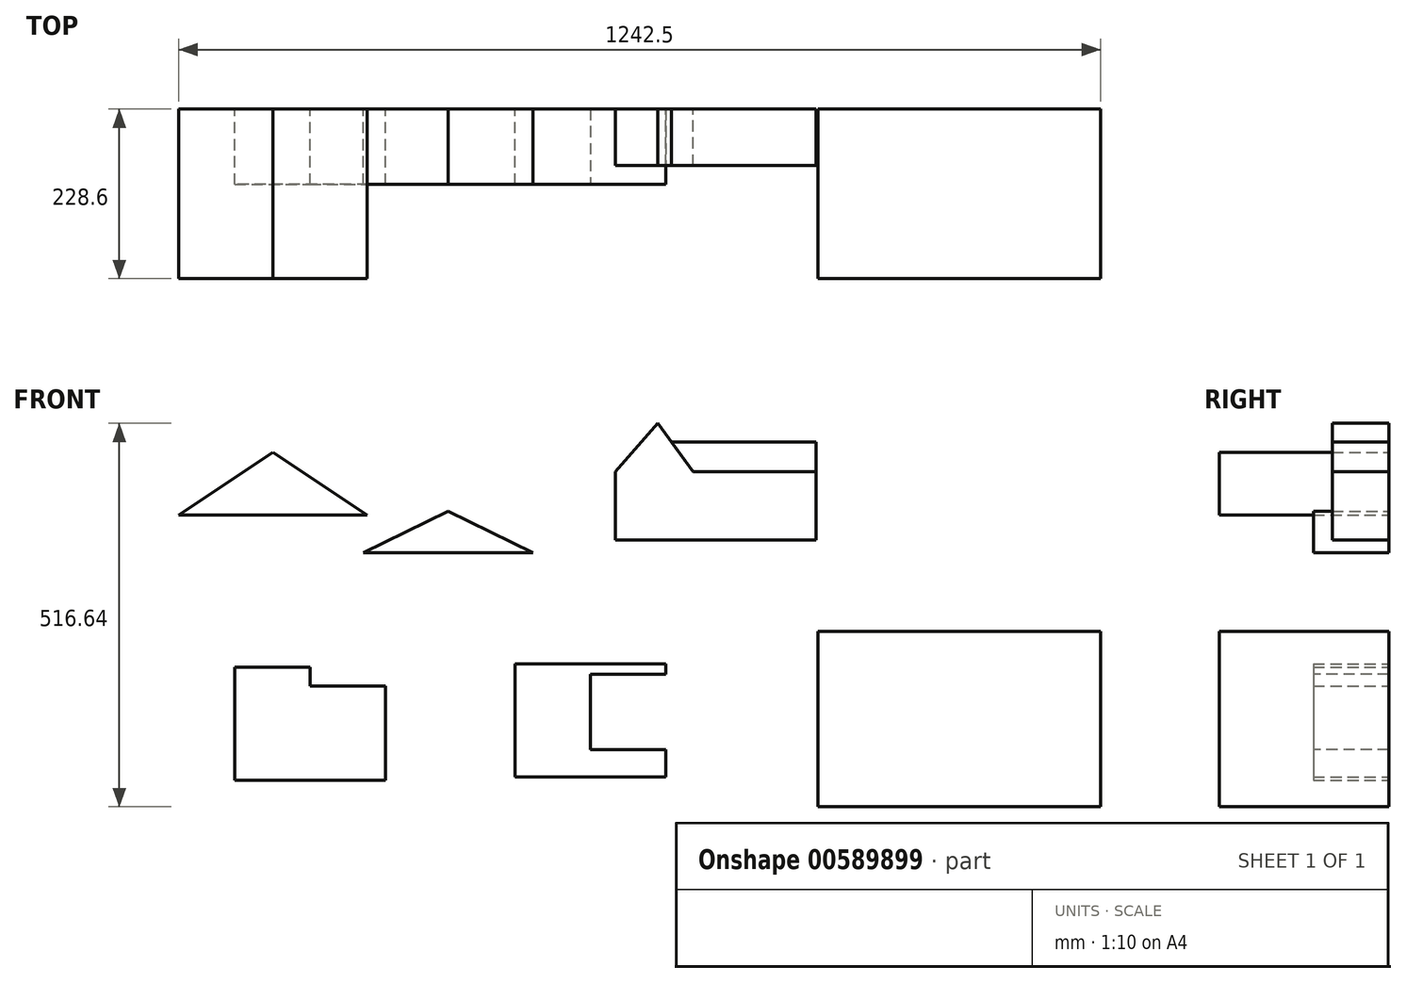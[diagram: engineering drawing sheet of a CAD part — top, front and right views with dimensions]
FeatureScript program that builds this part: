
annotation { "Feature Type Name" : "Feature", "Feature Type Description" : "" }
export const myFeature = defineFeature(function(context is Context, id is Id, definition is map)
    precondition{}
    {
        {
            var Q0;
            Q0=qCreatedBy(makeId("Front.planeOp"),FACE);
            var sketch = newSketch(context, id + "F0", { "sketchPlane" : qUnion([Q0])});
            skLineSegment(sketch, "E0", {"start": v(68.06, -35.27) * mm, "end": v(195.06, 48.97) * mm});
            skLineSegment(sketch, "E1", {"start": v(68.06, -35.27) * mm, "end": v(322.06, -35.27) * mm});
            skLineSegment(sketch, "E2", {"start": v(322.06, -35.27) * mm, "end": v(195.06, 48.97) * mm});
            skSolve(sketch);
        }
        {
            var Q0;
            Q0 = qSketchRegion(id + "F0", true);
            extrude(context, id + "F1", {"entities" : qUnion([Q0]), "depth" : 127 * mm, "offsetDistance" : 25.4 * mm});
        }
        {
            var Q0;
            Q0=makeQuery(id+"F1.opExtrude","CAP_FACE",FACE,{"disambiguationData":[OSD([sQuery(id+"F0.wireOp",EDGE,"E0"),sQuery(id+"F0.wireOp",EDGE,"E1"),sQuery(id+"F0.wireOp",EDGE,"E2")])],"isStart":false});
            var sketch = newSketch(context, id + "F2", { "sketchPlane" : qUnion([Q0])});
            skSolve(sketch);
        }
        {
            var Q0;
            Q0=makeQuery(id+"F2.imprint","IMPRINT",FACE,{"disambiguationData":[TD([[makeQuery(id+"F2.imprint","IMPRINT",EDGE,{"derivedFrom":makeQuery(id+"F1.opExtrude","CAP_EDGE",EDGE,{"disambiguationData":[OSD([sQuery(id+"F0.wireOp",EDGE,"E0")])],"isStart":false})}),-1.0]])]});
            var sketch = newSketch(context, id + "F3", { "sketchPlane" : qUnion([Q0])});
            skLineSegment(sketch, "E3", {"start": v(151.57, 21.29) * mm, "end": v(237, 21.29) * mm});
            skSolve(sketch);
        }
        {
            var Q0;
            Q0 = qSketchRegion(id + "F3", true);
            var Q1;
            Q1=makeQuery(id+"F2.imprint","IMPRINT",FACE,{"disambiguationData":[TD([[makeQuery(id+"F2.imprint","IMPRINT",EDGE,{"derivedFrom":makeQuery(id+"F1.opExtrude","CAP_EDGE",EDGE,{"disambiguationData":[OSD([sQuery(id+"F0.wireOp",EDGE,"E0")])],"isStart":false})}),-1.0]])]});
            extrude(context, id + "F4", {"entities" : qUnion([Q0, Q1]), "operationType" : NewBodyOperationType.ADD, "depth" : 76.2 * mm, "offsetDistance" : 25.4 * mm});
        }
        {
            var Q0;
            Q0=makeQuery(id+"F4.opExtrude","CAP_FACE",FACE,{"disambiguationData":[OSD([sQuery(id+"F0.wireOp",EDGE,"E0"),sQuery(id+"F0.wireOp",EDGE,"E1"),sQuery(id+"F0.wireOp",EDGE,"E2")])],"isStart":false});
            var sketch = newSketch(context, id + "F5", { "sketchPlane" : qUnion([Q0])});
            skSolve(sketch);
        }
        {
            var Q0;
            Q0 = qSketchRegion(id + "F5", true);
            var Q1;
            Q1=makeQuery(id+"F5.imprint","IMPRINT",FACE,{"disambiguationData":[TD([[makeQuery(id+"F5.imprint","IMPRINT",EDGE,{"derivedFrom":makeQuery(id+"F4.opExtrude","CAP_EDGE",EDGE,{"disambiguationData":[OSD([sQuery(id+"F0.wireOp",EDGE,"E0")])],"isStart":false})}),-1.0]])]});
            extrude(context, id + "F6", {"entities" : qUnion([Q0, Q1]), "operationType" : NewBodyOperationType.ADD, "depth" : 25.4 * mm, "offsetDistance" : 25.4 * mm});
        }
        {
            var Q0;
            Q0=qCreatedBy(makeId("Front.planeOp"),FACE);
            var sketch = newSketch(context, id + "F7", { "sketchPlane" : qUnion([Q0])});
            skLineSegment(sketch, "E4", {"start": v(431.32, -30.58) * mm, "end": v(317.02, -85.94) * mm});
            skLineSegment(sketch, "E5", {"start": v(431.32, -30.58) * mm, "end": v(545.62, -85.94) * mm});
            skLineSegment(sketch, "E6", {"start": v(545.62, -85.94) * mm, "end": v(317.02, -85.94) * mm});
            skSolve(sketch);
        }
        {
            var Q0;
            Q0 = qSketchRegion(id + "F7", true);
            extrude(context, id + "F8", {"entities" : qUnion([Q0]), "depth" : 101.6 * mm, "offsetDistance" : 25.4 * mm});
        }
        {
            var Q0;
            Q0=qCreatedBy(makeId("Front.planeOp"),FACE);
            var sketch = newSketch(context, id + "F9", { "sketchPlane" : qUnion([Q0])});
            skLineSegment(sketch, "E7", {"start": v(656.84, 22.7) * mm, "end": v(656.84, -69.03) * mm});
            skLineSegment(sketch, "E8", {"start": v(656.84, -69.03) * mm, "end": v(927.34, -69.03) * mm});
            skLineSegment(sketch, "E9", {"start": v(927.34, -69.03) * mm, "end": v(927.34, 84.7) * mm});
            skLineSegment(sketch, "E10", {"start": v(656.84, 22.7) * mm, "end": v(713.94, 88.22) * mm});
            skLineSegment(sketch, "E11", {"start": v(713.94, 88.22) * mm, "end": v(761.67, 22.7) * mm});
            skLineSegment(sketch, "E12", {"start": v(732.1, 63.3) * mm, "end": v(927.34, 63.3) * mm});
            skLineSegment(sketch, "E13", {"start": v(761.67, 22.7) * mm, "end": v(927.34, 22.7) * mm});
            skLineSegment(sketch, "E14", {"start": v(761.67, 22.7) * mm, "end": v(761.67, -69.03) * mm});
            skSolve(sketch);
        }
        {
            var Q0;
            {var subQ0=sQuery(id+"F9.wireOp",EDGE,"E12");Q0=makeQuery(id+"F9.imprint","IMPRINT",FACE,{"disambiguationData":[TD([[makeQuery(id+"F9.imprint","IMPRINT",EDGE,{"derivedFrom":subQ0}),-1.0]])]});}
            var sketch = newSketch(context, id + "F10", { "sketchPlane" : qUnion([Q0])});
            skSolve(sketch);
        }
        {
            var Q0;
            {var subQ4=sQuery(id+"F9.wireOp",EDGE,"E13");Q0=makeQuery(id+"F9.imprint","IMPRINT",FACE,{"disambiguationData":[TD([[makeQuery(id+"F9.imprint","IMPRINT",EDGE,{"derivedFrom":subQ4}),-1.0]])]});}
            var Q1;
            {var subQ4=sQuery(id+"F9.wireOp",EDGE,"E7");Q1=makeQuery(id+"F9.imprint","IMPRINT",FACE,{"disambiguationData":[TD([[makeQuery(id+"F9.imprint","IMPRINT",EDGE,{"derivedFrom":subQ4}),1.0]])]});}
            var Q2;
            {var subQ0=sQuery(id+"F9.wireOp",EDGE,"E12");Q2=makeQuery(id+"F10.imprint","IMPRINT",FACE,{"disambiguationData":[TD([[makeQuery(id+"F10.imprint","IMPRINT",EDGE,{"derivedFrom":makeQuery(id+"F9.imprint","IMPRINT",EDGE,{"derivedFrom":subQ0})}),-1.0]])]});}
            extrude(context, id + "F11", {"entities" : qUnion([Q0, Q1, Q2]), "depth" : 76.2 * mm, "offsetDistance" : 25.4 * mm});
        }
        {
            var Q0;
            Q0=qCreatedBy(makeId("Front.planeOp"),FACE);
            var sketch = newSketch(context, id + "F12", { "sketchPlane" : qUnion([Q0])});
            skLineSegment(sketch, "E15", {"start": v(143.28, -240.65) * mm, "end": v(143.28, -393.05) * mm});
            skLineSegment(sketch, "E16", {"start": v(143.28, -240.65) * mm, "end": v(244.88, -240.65) * mm});
            skLineSegment(sketch, "E17", {"start": v(244.88, -240.65) * mm, "end": v(244.88, -266.05) * mm});
            skLineSegment(sketch, "E18", {"start": v(244.88, -266.05) * mm, "end": v(346.48, -266.05) * mm});
            skLineSegment(sketch, "E19", {"start": v(346.48, -266.05) * mm, "end": v(346.48, -393.05) * mm});
            skLineSegment(sketch, "E20", {"start": v(346.48, -393.05) * mm, "end": v(143.28, -393.05) * mm});
            skSolve(sketch);
        }
        {
            var Q0;
            Q0 = qSketchRegion(id + "F12", true);
            extrude(context, id + "F13", {"entities" : qUnion([Q0]), "depth" : 101.6 * mm, "offsetDistance" : 25.4 * mm});
        }
        {
            var Q0;
            Q0=qCreatedBy(makeId("Front.planeOp"),FACE);
            var sketch = newSketch(context, id + "F14", { "sketchPlane" : qUnion([Q0])});
            skLineSegment(sketch, "E21.bottom", {"start": v(521.15, -236.11) * mm, "end": v(724.35, -236.11) * mm});
            skLineSegment(sketch, "E21.top", {"start": v(521.15, -388.51) * mm, "end": v(724.35, -388.51) * mm});
            skLineSegment(sketch, "E21.left", {"start": v(521.15, -236.11) * mm, "end": v(521.15, -388.51) * mm});
            skLineSegment(sketch, "E21.right", {"start": v(724.35, -236.11) * mm, "end": v(724.35, -388.51) * mm});
            skLineSegment(sketch, "E22", {"start": v(724.35, -259.36) * mm, "end": v(622.75, -259.36) * mm});
            skLineSegment(sketch, "E23", {"start": v(622.75, -259.36) * mm, "end": v(622.75, -360.96) * mm});
            skLineSegment(sketch, "E24", {"start": v(622.75, -360.96) * mm, "end": v(724.35, -360.96) * mm});
            skSolve(sketch);
        }
        {
            var Q0;
            {var subQ1=sQuery(id+"F14.wireOp",EDGE,"E21.bottom");Q0=makeQuery(id+"F14.imprint","IMPRINT",FACE,{"disambiguationData":[TD([[makeQuery(id+"F14.imprint","IMPRINT",EDGE,{"derivedFrom":subQ1}),-1.0]])]});}
            var Q1;
            {var subQ0=sQuery(id+"F14.wireOp",EDGE,"E22");Q1=makeQuery(id+"F14.imprint","IMPRINT",FACE,{"disambiguationData":[TD([[makeQuery(id+"F14.imprint","IMPRINT",EDGE,{"derivedFrom":subQ0}),1.0]])]});}
            extrude(context, id + "F15", {"entities" : qUnion([Q0, Q1]), "depth" : 101.6 * mm, "offsetDistance" : 25.4 * mm});
        }
        {
            var Q0;
            Q0=makeQuery(id+"F15.opExtrude","CAP_FACE",FACE,{"disambiguationData":[OSD([sQuery(id+"F14.wireOp",EDGE,"E21.bottom"),sQuery(id+"F14.wireOp",EDGE,"E21.top"),sQuery(id+"F14.wireOp",EDGE,"E21.left"),sQuery(id+"F14.wireOp",EDGE,"E21.right")])],"isStart":false});
            var sketch = newSketch(context, id + "F16", { "sketchPlane" : qUnion([Q0])});
            skLineSegment(sketch, "E25", {"start": v(724.35, -250.35) * mm, "end": v(622.75, -250.35) * mm});
            skLineSegment(sketch, "E26", {"start": v(622.75, -250.35) * mm, "end": v(622.75, -351.95) * mm});
            skLineSegment(sketch, "E27", {"start": v(622.75, -351.95) * mm, "end": v(724.35, -351.95) * mm});
            skSolve(sketch);
        }
        {
            var Q0;
            {var subQ0=sQuery(id+"F16.wireOp",EDGE,"E25");Q0=makeQuery(id+"F16.imprint","IMPRINT",FACE,{"disambiguationData":[TD([[makeQuery(id+"F16.imprint","IMPRINT",EDGE,{"derivedFrom":subQ0}),1.0]])]});}
            extrude(context, id + "F17", {"entities" : qUnion([Q0]), "operationType" : NewBodyOperationType.REMOVE, "oppositeDirection" : true, "depth" : 127 * mm, "offsetDistance" : 25.4 * mm});
        }
        {
            var Q0;
            Q0=qCreatedBy(makeId("Front.planeOp"),FACE);
            var sketch = newSketch(context, id + "F18", { "sketchPlane" : qUnion([Q0])});
            skLineSegment(sketch, "E28.bottom", {"start": v(929.42, -192.48) * mm, "end": v(1310.56, -192.48) * mm});
            skLineSegment(sketch, "E28.top", {"start": v(929.42, -428.42) * mm, "end": v(1310.56, -428.42) * mm});
            skLineSegment(sketch, "E28.left", {"start": v(929.42, -192.48) * mm, "end": v(929.42, -428.42) * mm});
            skLineSegment(sketch, "E28.right", {"start": v(1310.56, -192.48) * mm, "end": v(1310.56, -428.42) * mm});
            skSolve(sketch);
        }
        {
            var Q0;
            Q0=makeQuery(id+"F18.imprint","IMPRINT",FACE,{"disambiguationData":[TD([[makeQuery(id+"F18.imprint","IMPRINT",EDGE,{"derivedFrom":sQuery(id+"F18.wireOp",EDGE,"E28.bottom")}),-1.0]])]});
            var sketch = newSketch(context, id + "F19", { "sketchPlane" : qUnion([Q0])});
            skSolve(sketch);
        }
        {
            var Q0;
            Q0 = qSketchRegion(id + "F18", true);
            extrude(context, id + "F20", {"entities" : qUnion([Q0]), "depth" : 127 * mm, "offsetDistance" : 25.4 * mm});
        }
        {
            var Q0;
            Q0=makeQuery(id+"F20.opExtrude","CAP_FACE",FACE,{"disambiguationData":[OSD([sQuery(id+"F18.wireOp",EDGE,"E28.bottom"),sQuery(id+"F18.wireOp",EDGE,"E28.top"),sQuery(id+"F18.wireOp",EDGE,"E28.left"),sQuery(id+"F18.wireOp",EDGE,"E28.right")])],"isStart":false});
            var sketch = newSketch(context, id + "F21", { "sketchPlane" : qUnion([Q0])});
            skSolve(sketch);
        }
        {
            var Q0;
            Q0=qCreatedBy(makeId("Front.planeOp"),FACE);
            var sketch = newSketch(context, id + "F22", { "sketchPlane" : qUnion([Q0])});
            skArc(sketch, "E29", {"start": v(1051.97, -192.73) * mm, "mid": v(1126.54, -262.55) * mm, "end": v(1203.56, -195.43) * mm});
            skSolve(sketch);
        }
        {
            var Q0;
            Q0 = qSketchRegion(id + "F22", true);
            var Q1;
            Q1=makeQuery(id+"F21.imprint","IMPRINT",FACE,{"disambiguationData":[TD([[makeQuery(id+"F21.imprint","IMPRINT",EDGE,{"derivedFrom":makeQuery(id+"F20.opExtrude","CAP_EDGE",EDGE,{"disambiguationData":[OSD([sQuery(id+"F18.wireOp",EDGE,"E28.bottom")])],"isStart":false})}),-1.0]])]});
            var Q2;
            Q2=makeQuery(id+"F19.imprint","IMPRINT",FACE,{"disambiguationData":[TD([[makeQuery(id+"F19.imprint","IMPRINT",EDGE,{"derivedFrom":makeQuery(id+"F18.imprint","IMPRINT",EDGE,{"derivedFrom":sQuery(id+"F18.wireOp",EDGE,"E28.bottom")})}),-1.0]])]});
            extrude(context, id + "F23", {"entities" : qUnion([Q0, Q1, Q2]), "operationType" : NewBodyOperationType.ADD, "depth" : 101.6 * mm, "offsetDistance" : 25.4 * mm});
        }
    });
